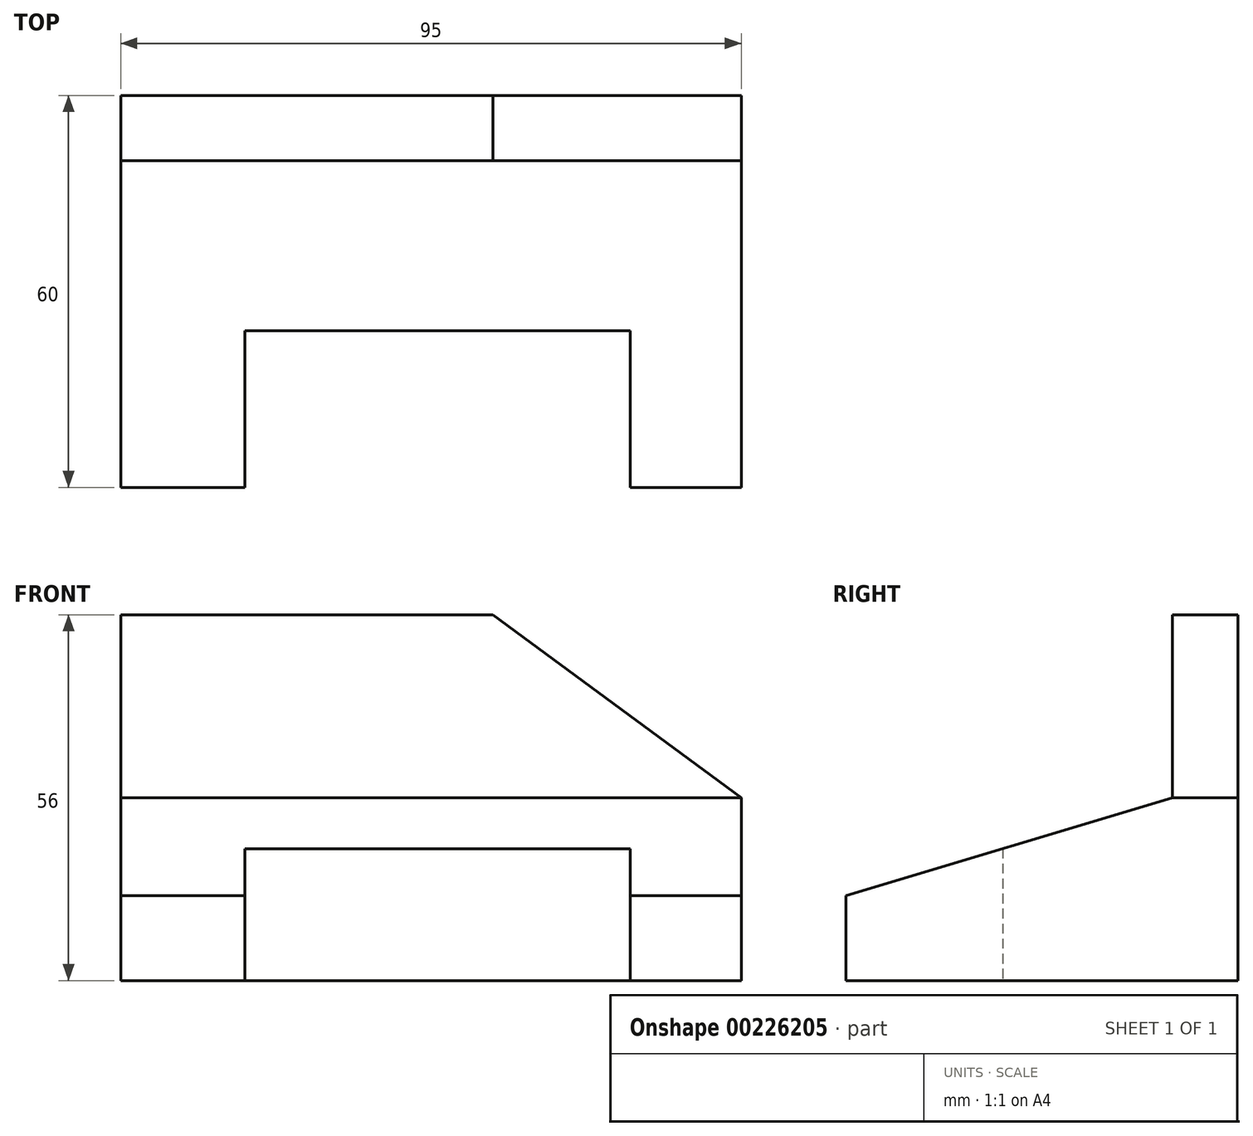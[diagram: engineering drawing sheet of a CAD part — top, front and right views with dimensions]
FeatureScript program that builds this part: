
annotation { "Feature Type Name" : "Feature", "Feature Type Description" : "" }
export const myFeature = defineFeature(function(context is Context, id is Id, definition is map)
    precondition{}
    {
        {
            var Q0;
            Q0=qCreatedBy(makeId("Right.planeOp"),FACE);
            var sketch = newSketch(context, id + "F0", { "sketchPlane" : qUnion([Q0])});
            skLineSegment(sketch, "E0", {"start": v(0, 0) * mm, "end": v(0, 56) * mm});
            skLineSegment(sketch, "E1", {"start": v(0, 56) * mm, "end": v(-10, 56) * mm});
            skLineSegment(sketch, "E2", {"start": v(-10, 56) * mm, "end": v(-10, 28) * mm});
            skLineSegment(sketch, "E3", {"start": v(-10, 28) * mm, "end": v(-60, 13) * mm});
            skLineSegment(sketch, "E4", {"start": v(-60, 13) * mm, "end": v(-60, 0) * mm});
            skLineSegment(sketch, "E5", {"start": v(-60, 0) * mm, "end": v(0, 0) * mm});
            skSolve(sketch);
        }
        {
            var Q0;
            Q0=qSketchRegion(id+"F0",true);
            extrude(context, id + "F1", {"entities" : qUnion([Q0]), "depth" : 95 * mm});
        }
        {
            var Q0;
            Q0=makeQuery(id+"F1.opExtrude","SWEPT_FACE",FACE,{"disambiguationData":[OSD([sQuery(id+"F0.wireOp",EDGE,"E2")])]});
            var sketch = newSketch(context, id + "F2", { "sketchPlane" : qUnion([Q0])});
            skLineSegment(sketch, "E6", {"start": v(95, 28) * mm, "end": v(57, 56) * mm});
            skSolve(sketch);
        }
        {
            var Q0;
            {var subQ0=sQuery(id+"F2.wireOp",EDGE,"E6");Q0=makeQuery(id+"F2.imprint","IMPRINT",FACE,{"disambiguationData":[TD([[makeQuery(id+"F2.imprint","IMPRINT",EDGE,{"derivedFrom":subQ0}),-1.0]])]});}
            extrude(context, id + "F3", {"entities" : qUnion([Q0]), "operationType" : NewBodyOperationType.REMOVE, "endBound" : BoundingType.THROUGH_ALL, "oppositeDirection" : true, "depth" : 25 * mm});
        }
        {
            var Q0;
            Q0=makeQuery(id+"F1.opExtrude","SWEPT_FACE",FACE,{"disambiguationData":[OSD([sQuery(id+"F0.wireOp",EDGE,"E5")])]});
            var sketch = newSketch(context, id + "F4", { "sketchPlane" : qUnion([Q0])});
            skLineSegment(sketch, "E7.bottom", {"start": v(19, 60) * mm, "end": v(78, 60) * mm});
            skLineSegment(sketch, "E7.top", {"start": v(19, 36) * mm, "end": v(78, 36) * mm});
            skLineSegment(sketch, "E7.left", {"start": v(19, 60) * mm, "end": v(19, 36) * mm});
            skLineSegment(sketch, "E7.right", {"start": v(78, 60) * mm, "end": v(78, 36) * mm});
            skSolve(sketch);
        }
        {
            var Q0;
            Q0=qSketchRegion(id+"F4",true);
            extrude(context, id + "F5", {"entities" : qUnion([Q0]), "operationType" : NewBodyOperationType.REMOVE, "endBound" : BoundingType.THROUGH_ALL, "oppositeDirection" : true, "depth" : 25 * mm});
        }
    });
